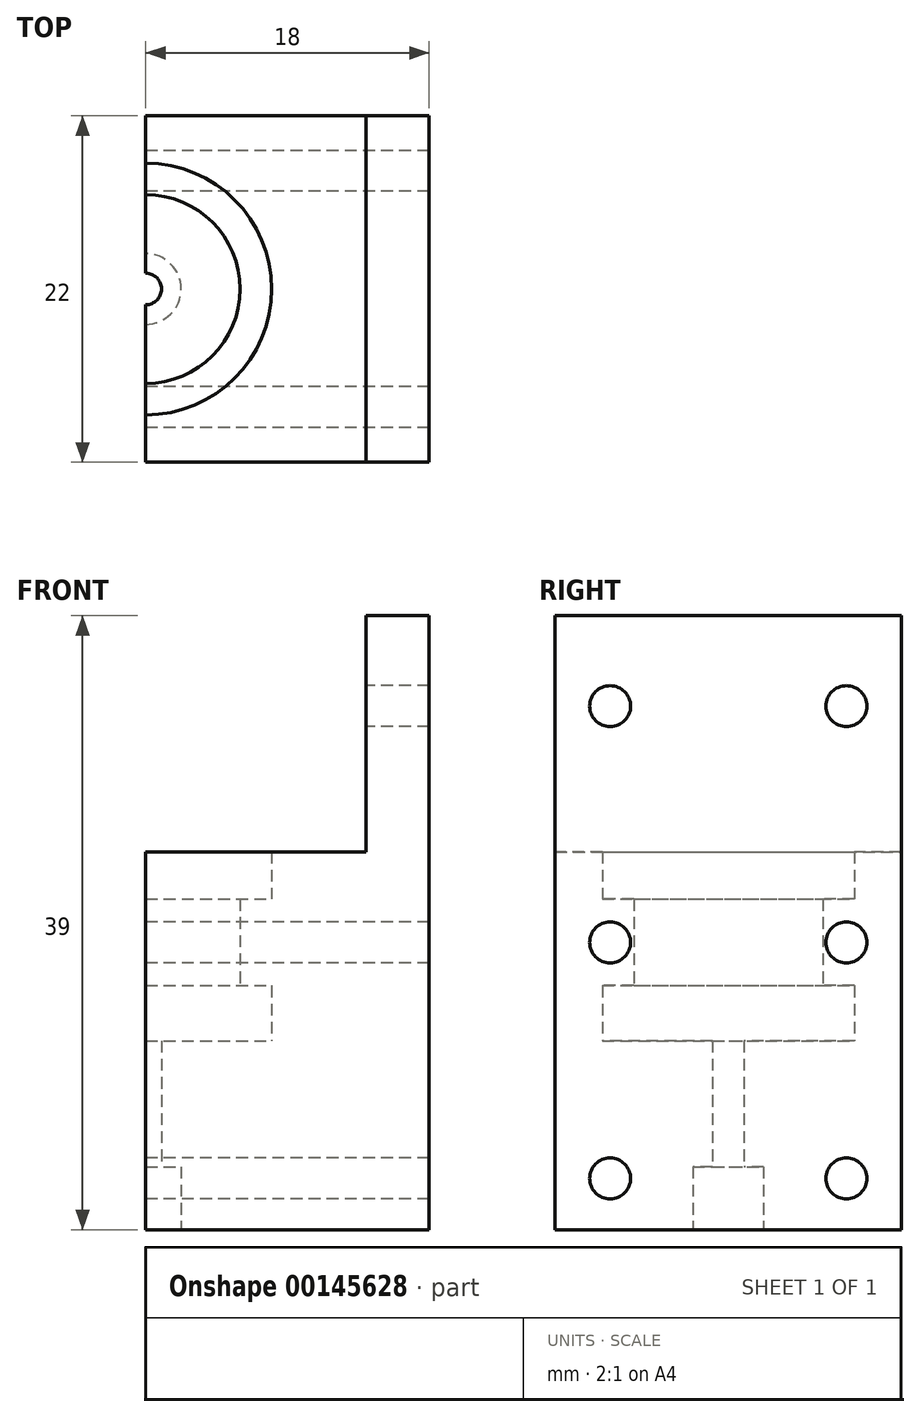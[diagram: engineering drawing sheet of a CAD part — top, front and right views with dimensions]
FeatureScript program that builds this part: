
annotation { "Feature Type Name" : "Feature", "Feature Type Description" : "" }
export const myFeature = defineFeature(function(context is Context, id is Id, definition is map)
    precondition{}
    {
        {
            assignVariable(context, id + "F0", {"name" : "height", "anyValue" : 24});
        }
        {
            var Q0;
            Q0=qCreatedBy(makeId("Top.planeOp"),FACE);
            var sketch = newSketch(context, id + "F1", { "sketchPlane" : qUnion([Q0])});
            skLineSegment(sketch, "E0.left", {"start": v(-11, 11) * mm, "end": v(-11, -11) * mm});
            skLineSegment(sketch, "E0.right", {"start": v(11, 11) * mm, "end": v(11, -11) * mm});
            skPoint(sketch, "E0.middle", {"position": v(0, 0) * mm});
            skCircle(sketch, "E1", {"center": v(0, 0) * mm, "radius": 8 * mm});
            skCircle(sketch, "E2", {"center": v(0, 0) * mm, "radius": 6 * mm});
            skCircle(sketch, "E3", {"center": v(0, 0) * mm, "radius": 2.25 * mm});
            skCircle(sketch, "E4", {"center": v(0, 0) * mm, "radius": 1 * mm});
            skLineSegment(sketch, "E5", {"start": v(0, 11) * mm, "end": v(0, -11) * mm});
            skLineSegment(sketch, "E6", {"start": v(0, -11) * mm, "end": v(11, -11) * mm});
            skLineSegment(sketch, "E7", {"start": v(-11, -11) * mm, "end": v(0, -11) * mm});
            skLineSegment(sketch, "E8", {"start": v(0, 11) * mm, "end": v(11, 11) * mm});
            skLineSegment(sketch, "E9", {"start": v(-11, 11) * mm, "end": v(0, 11) * mm});
            skLineSegment(sketch, "E10", {"start": v(11, -11) * mm, "end": v(14, -11) * mm});
            skLineSegment(sketch, "E11", {"start": v(14, -11) * mm, "end": v(14, 11) * mm});
            skLineSegment(sketch, "E12", {"start": v(14, 11) * mm, "end": v(11, 11) * mm});
            skLineSegment(sketch, "E13", {"start": v(14, -11) * mm, "end": v(18, -11) * mm});
            skLineSegment(sketch, "E14", {"start": v(18, -11) * mm, "end": v(18, 11) * mm});
            skLineSegment(sketch, "E15", {"start": v(18, 11) * mm, "end": v(14, 11) * mm});
            skSolve(sketch);
        }
        {
            var Q0;
            {var subQ6=sQuery(id+"F1.wireOp",EDGE,"E0.right");Q0=makeQuery(id+"F1.imprint","IMPRINT",FACE,{"disambiguationData":[TD([[makeQuery(id+"F1.imprint","IMPRINT",EDGE,{"derivedFrom":subQ6}),-1.0]])]});}
            extrude(context, id + "F2", {"entities" : qUnion([Q0]), "depth" : (getVariable(context, 'height')) * mm});
        }
        {
            var Q0;
            Q0=makeQuery(id+"F1.imprint","IMPRINT",FACE,{"disambiguationData":[TD([[makeQuery(id+"F1.imprint","IMPRINT",EDGE,{"derivedFrom":sQuery(id+"F1.wireOp",EDGE,"E0.right")}),1.0]])]});
            extrude(context, id + "F3", {"entities" : qUnion([Q0]), "operationType" : NewBodyOperationType.ADD, "depth" : 24 * mm});
        }
        {
            var Q0;
            Q0=makeQuery(id+"F1.imprint","IMPRINT",FACE,{"disambiguationData":[TD([[makeQuery(id+"F1.imprint","IMPRINT",EDGE,{"derivedFrom":sQuery(id+"F1.wireOp",EDGE,"E11")}),-1.0]])]});
            extrude(context, id + "F4", {"entities" : qUnion([Q0]), "operationType" : NewBodyOperationType.ADD, "depth" : 39 * mm});
        }
        {
            var Q0;
            {var subQ0=sQuery(id+"F1.wireOp",EDGE,"E5");var subQ1=sQuery(id+"F1.wireOp",EDGE,"E1");var subQ2=makeQuery(id+"F1.imprint","INTERSECT",VERTEX,{"disambiguationData":[OD(0.0)],"derivedFrom":[subQ1,subQ0]});Q0=makeQuery(id+"F1.imprint","IMPRINT",FACE,{"disambiguationData":[TD([[makeQuery(id+"F1.imprint","IMPRINT",EDGE,{"disambiguationData":[TD([[subQ2,1.0]])],"derivedFrom":subQ1}),1.0]])]});}
            extrude(context, id + "F5", {"entities" : qUnion([Q0]), "operationType" : NewBodyOperationType.ADD, "depth" : (getVariable(context, 'height') - 3) * mm});
        }
        {
            var Q0;
            {var subQ0=sQuery(id+"F1.wireOp",EDGE,"E5");var subQ1=sQuery(id+"F1.wireOp",EDGE,"E1");var subQ2=makeQuery(id+"F1.imprint","INTERSECT",VERTEX,{"disambiguationData":[OD(0.0)],"derivedFrom":[subQ1,subQ0]});Q0=makeQuery(id+"F1.imprint","IMPRINT",FACE,{"disambiguationData":[TD([[makeQuery(id+"F1.imprint","IMPRINT",EDGE,{"disambiguationData":[TD([[subQ2,1.0]])],"derivedFrom":subQ1}),1.0]])]});}
            var Q1;
            {var subQ0=sQuery(id+"F1.wireOp",EDGE,"E5");var subQ1=sQuery(id+"F1.wireOp",EDGE,"E1");var subQ2=makeQuery(id+"F1.imprint","INTERSECT",VERTEX,{"disambiguationData":[OD(0.0)],"derivedFrom":[subQ1,subQ0]});Q1=makeQuery(id+"F1.imprint","IMPRINT",FACE,{"disambiguationData":[TD([[makeQuery(id+"F1.imprint","IMPRINT",EDGE,{"disambiguationData":[TD([[subQ2,-1.0]])],"derivedFrom":subQ1}),1.0]])]});}
            extrude(context, id + "F6", {"entities" : qUnion([Q0, Q1]), "operationType" : NewBodyOperationType.REMOVE, "depth" : (getVariable(context, 'height') - 3 - 5.5) * mm});
        }
        {
            var Q0;
            {var subQ0=sQuery(id+"F1.wireOp",EDGE,"E5");var subQ1=sQuery(id+"F1.wireOp",EDGE,"E1");var subQ2=makeQuery(id+"F1.imprint","INTERSECT",VERTEX,{"disambiguationData":[OD(0.0)],"derivedFrom":[subQ1,subQ0]});Q0=makeQuery(id+"F1.imprint","IMPRINT",FACE,{"disambiguationData":[TD([[makeQuery(id+"F1.imprint","IMPRINT",EDGE,{"disambiguationData":[TD([[subQ2,1.0]])],"derivedFrom":subQ1}),1.0]])]});}
            var Q1;
            {var subQ0=sQuery(id+"F1.wireOp",EDGE,"E5");var subQ1=sQuery(id+"F1.wireOp",EDGE,"E2");var subQ2=makeQuery(id+"F1.imprint","INTERSECT",VERTEX,{"disambiguationData":[OD(0.0)],"derivedFrom":[subQ1,subQ0]});Q1=makeQuery(id+"F1.imprint","IMPRINT",FACE,{"disambiguationData":[TD([[makeQuery(id+"F1.imprint","IMPRINT",EDGE,{"disambiguationData":[TD([[subQ2,1.0]])],"derivedFrom":subQ1}),1.0]])]});}
            var Q2;
            {var subQ0=sQuery(id+"F1.wireOp",EDGE,"E5");var subQ1=sQuery(id+"F1.wireOp",EDGE,"E3");var subQ2=makeQuery(id+"F1.imprint","INTERSECT",VERTEX,{"disambiguationData":[OD(0.0)],"derivedFrom":[subQ1,subQ0]});Q2=makeQuery(id+"F1.imprint","IMPRINT",FACE,{"disambiguationData":[TD([[makeQuery(id+"F1.imprint","IMPRINT",EDGE,{"disambiguationData":[TD([[subQ2,1.0]])],"derivedFrom":subQ1}),1.0]])]});}
            extrude(context, id + "F7", {"entities" : qUnion([Q0, Q1, Q2]), "operationType" : NewBodyOperationType.ADD, "depth" : (getVariable(context, 'height') - 3 - 5.5 - 3.5) * mm});
        }
        {
            var Q0;
            {var subQ0=sQuery(id+"F1.wireOp",EDGE,"E5");var subQ1=sQuery(id+"F1.wireOp",EDGE,"E3");var subQ2=makeQuery(id+"F1.imprint","INTERSECT",VERTEX,{"disambiguationData":[OD(0.0)],"derivedFrom":[subQ1,subQ0]});Q0=makeQuery(id+"F1.imprint","IMPRINT",FACE,{"disambiguationData":[TD([[makeQuery(id+"F1.imprint","IMPRINT",EDGE,{"disambiguationData":[TD([[subQ2,1.0]])],"derivedFrom":subQ1}),1.0]])]});}
            var Q1;
            {var subQ0=sQuery(id+"F1.wireOp",EDGE,"E5");var subQ1=sQuery(id+"F1.wireOp",EDGE,"E3");var subQ2=makeQuery(id+"F1.imprint","INTERSECT",VERTEX,{"disambiguationData":[OD(0.0)],"derivedFrom":[subQ1,subQ0]});Q1=makeQuery(id+"F1.imprint","IMPRINT",FACE,{"disambiguationData":[TD([[makeQuery(id+"F1.imprint","IMPRINT",EDGE,{"disambiguationData":[TD([[subQ2,-1.0]])],"derivedFrom":subQ1}),1.0]])]});}
            extrude(context, id + "F8", {"entities" : qUnion([Q0, Q1]), "operationType" : NewBodyOperationType.REMOVE, "depth" : 4 * mm});
        }
        {
            var Q0;
            {var subQ0=sQuery(id+"F1.wireOp",EDGE,"E5");var subQ1=makeQuery(id+"F1.imprint","INTERSECT",VERTEX,{"disambiguationData":[OD(0.0)],"derivedFrom":[sQuery(id+"F1.wireOp",EDGE,"E3"),subQ0]});var subQ2=makeQuery(id+"F1.imprint","INTERSECT",VERTEX,{"disambiguationData":[OD(0.0)],"derivedFrom":[sQuery(id+"F1.wireOp",EDGE,"E2"),subQ0]});var subQ3=makeQuery(id+"F1.imprint","INTERSECT",VERTEX,{"disambiguationData":[OD(0.0)],"derivedFrom":[sQuery(id+"F1.wireOp",EDGE,"E1"),subQ0]});var subQ4=makeQuery(id+"F1.imprint","IMPRINT",EDGE,{"disambiguationData":[TD([[subQ3,-1.0]])],"derivedFrom":subQ0});Q0=makeQuery(id+"F7.boolean.opBoolean","MERGE",FACE,{"derivedFrom":[makeQuery(id+"F5.boolean.opBoolean","MERGE",FACE,{"derivedFrom":[makeQuery(id+"F2.opExtrude","SWEPT_FACE",FACE,{"disambiguationData":[OSD([subQ0]),TDD([makeQuery(id+"F1.imprint","IMPRINT",EDGE,{"disambiguationData":[TD([[makeQuery(id+"F1.imprint","INTERSECT",VERTEX,{"derivedFrom":[sQuery(id+"F1.wireOp",EDGE,"E0.bottom"),subQ0]}),-1.0]])],"derivedFrom":subQ0})])]}),makeQuery(id+"F5.opExtrude","SWEPT_FACE",FACE,{"disambiguationData":[OSD([subQ0]),TDD([subQ4])]})]}),makeQuery(id+"F7.opExtrude","SWEPT_FACE",FACE,{"disambiguationData":[OSD([subQ0]),TDD([subQ4,makeQuery(id+"F1.imprint","IMPRINT",EDGE,{"disambiguationData":[TD([[subQ2,-1.0]])],"derivedFrom":subQ0}),makeQuery(id+"F1.imprint","IMPRINT",EDGE,{"disambiguationData":[TD([[subQ1,-1.0]])],"derivedFrom":subQ0})])]})]});}
            var sketch = newSketch(context, id + "F9", { "sketchPlane" : qUnion([Q0])});
            skPoint(sketch, "E16", {"position": v(-6, 18.25) * mm});
            skPoint(sketch, "E17", {"position": v(6, 18.25) * mm});
            skLineSegment(sketch, "E18", {"start": v(-6, 18.25) * mm, "end": v(6, 18.25) * mm, "construction": true});
            skLineSegment(sketch, "E19", {"start": v(6, 18.25) * mm, "end": v(7.5, 18.25) * mm, "construction": true});
            skLineSegment(sketch, "E20", {"start": v(-6, 18.25) * mm, "end": v(-7.5, 18.25) * mm, "construction": true});
            skCircle(sketch, "E21", {"center": v(-7.5, 18.25) * mm, "radius": 1.3 * mm});
            skCircle(sketch, "E22", {"center": v(7.5, 18.25) * mm, "radius": 1.3 * mm});
            skLineSegment(sketch, "E23", {"start": v(-7.5, 18.25) * mm, "end": v(-7.5, 3.25) * mm, "construction": true});
            skLineSegment(sketch, "E24", {"start": v(7.5, 18.25) * mm, "end": v(7.5, 3.25) * mm, "construction": true});
            skCircle(sketch, "E25", {"center": v(-7.5, 3.25) * mm, "radius": 1.3 * mm});
            skCircle(sketch, "E26", {"center": v(7.5, 3.25) * mm, "radius": 1.3 * mm});
            skLineSegment(sketch, "E27", {"start": v(-7.5, 18.25) * mm, "end": v(-7.5, 33.25) * mm, "construction": true});
            skLineSegment(sketch, "E28", {"start": v(7.5, 18.25) * mm, "end": v(7.5, 33.25) * mm, "construction": true});
            skCircle(sketch, "E29", {"center": v(-7.5, 33.25) * mm, "radius": 1.3 * mm});
            skCircle(sketch, "E30", {"center": v(7.5, 33.25) * mm, "radius": 1.3 * mm});
            skSolve(sketch);
        }
        {
            var Q0;
            Q0=makeQuery(id+"F9.imprint","IMPRINT",FACE,{"disambiguationData":[TD([[makeQuery(id+"F9.imprint","IMPRINT",EDGE,{"derivedFrom":sQuery(id+"F9.wireOp",EDGE,"E21")}),1.0]])]});
            var Q1;
            Q1=makeQuery(id+"F9.imprint","IMPRINT",FACE,{"disambiguationData":[TD([[makeQuery(id+"F9.imprint","IMPRINT",EDGE,{"derivedFrom":sQuery(id+"F9.wireOp",EDGE,"E22")}),1.0]])]});
            var Q2;
            Q2=makeQuery(id+"F9.imprint","IMPRINT",FACE,{"disambiguationData":[TD([[makeQuery(id+"F9.imprint","IMPRINT",EDGE,{"derivedFrom":sQuery(id+"F9.wireOp",EDGE,"E26")}),1.0]])]});
            var Q3;
            Q3=makeQuery(id+"F9.imprint","IMPRINT",FACE,{"disambiguationData":[TD([[makeQuery(id+"F9.imprint","IMPRINT",EDGE,{"derivedFrom":sQuery(id+"F9.wireOp",EDGE,"E25")}),1.0]])]});
            var Q4;
            Q4=makeQuery(id+"F9.imprint","IMPRINT",FACE,{"disambiguationData":[TD([[makeQuery(id+"F9.imprint","IMPRINT",EDGE,{"derivedFrom":sQuery(id+"F9.wireOp",EDGE,"E29")}),1.0]])]});
            var Q5;
            Q5=makeQuery(id+"F9.imprint","IMPRINT",FACE,{"disambiguationData":[TD([[makeQuery(id+"F9.imprint","IMPRINT",EDGE,{"derivedFrom":sQuery(id+"F9.wireOp",EDGE,"E30")}),1.0]])]});
            extrude(context, id + "F10", {"entities" : qUnion([Q0, Q1, Q2, Q3, Q4, Q5]), "operationType" : NewBodyOperationType.REMOVE, "endBound" : BoundingType.THROUGH_ALL, "oppositeDirection" : true, "depth" : 25 * mm});
        }
    });
